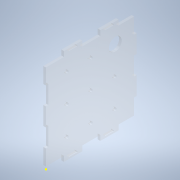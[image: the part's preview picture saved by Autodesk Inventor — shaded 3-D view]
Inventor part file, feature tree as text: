
AUTODESK INVENTOR PART (.ipt)
format: ipt  version: 2020 (Build 240168000, 168)  size: 195,584 bytes
history: native  units: mm
features: sketch x11, hole x9, extrude x1
ambient origin geometry x8: Origin, YZ Plane, XZ Plane, XY Plane, X Axis, Y Axis, Z Axis, Center Point
bodies: Solid1 (feature_tree)
feature tree (21):
  extrude  "Extrusion1"  Depth=3.0mm
  hole  "Hole2"  [1 undecoded]
  hole  "Hole3"  [1 undecoded]
  hole  "Hole4"  [1 undecoded]
  hole  "Hole5"  [1 undecoded]
  hole  "Hole6"  [1 undecoded]
  hole  "Hole7"  [1 undecoded]
  hole  "Hole8"  [1 undecoded]
  hole  "Hole9"  [1 undecoded]
  sketch  "Sketch11"  dims[d87=15.0mm d88=6.0mm d89=4.0mm d90=2.0mm d91=90.0deg d92=8.0mm d93=20.594885mm d94=1.0mm]
  hole  "Hole10"  [1 undecoded]
  sketch  "Sketch1"  dims[d4=3.0mm d5=0.0mm d22=3.0mm]
  sketch  "Sketch3"  dims[d23=3.0mm d24=6.0mm d25=4.0mm d26=2.0mm d27=90.0deg d28=8.0mm d29=20.594885mm d30=3.0mm]
  sketch  "Sketch4"  dims[d31=3.0mm d32=6.0mm d33=4.0mm d34=2.0mm d35=90.0deg d36=8.0mm d37=20.594885mm d38=3.0mm]
  sketch  "Sketch5"  dims[d39=3.0mm d40=6.0mm d41=4.0mm d42=2.0mm d43=90.0deg d44=8.0mm d45=20.594885mm d46=3.0mm]
  sketch  "Sketch6"  dims[d47=3.0mm d48=6.0mm d49=4.0mm d50=2.0mm d51=90.0deg d52=8.0mm d53=20.594885mm d54=3.0mm]
  sketch  "Sketch7"  dims[d55=3.0mm d56=6.0mm d57=4.0mm d58=2.0mm d59=90.0deg d60=8.0mm d61=20.594885mm d62=3.0mm]
  sketch  "Sketch8"  dims[d63=3.0mm d64=6.0mm d65=4.0mm d66=2.0mm d67=90.0deg d68=8.0mm d69=20.594885mm d70=3.0mm]
  sketch  "Sketch9"  dims[d71=3.0mm d72=6.0mm d73=4.0mm d74=2.0mm d75=90.0deg d76=8.0mm d77=20.594885mm d78=3.0mm]
  sketch  "Sketch10"  dims[d79=3.0mm d80=6.0mm d81=4.0mm d82=2.0mm d83=90.0deg d84=8.0mm d85=20.594885mm d86=3.0mm]
  sketch  "Sketch12"  dims[d95=10.0mm d96=10.0mm d97=1.0mm d98=10.0mm d99=1.0mm d100=10.0mm]
note: 9 required parameter values undecoded (feature->parameter linkage not recoverable at this tier; creation-order binding heuristic only, values carry confidence <= 0.55)
